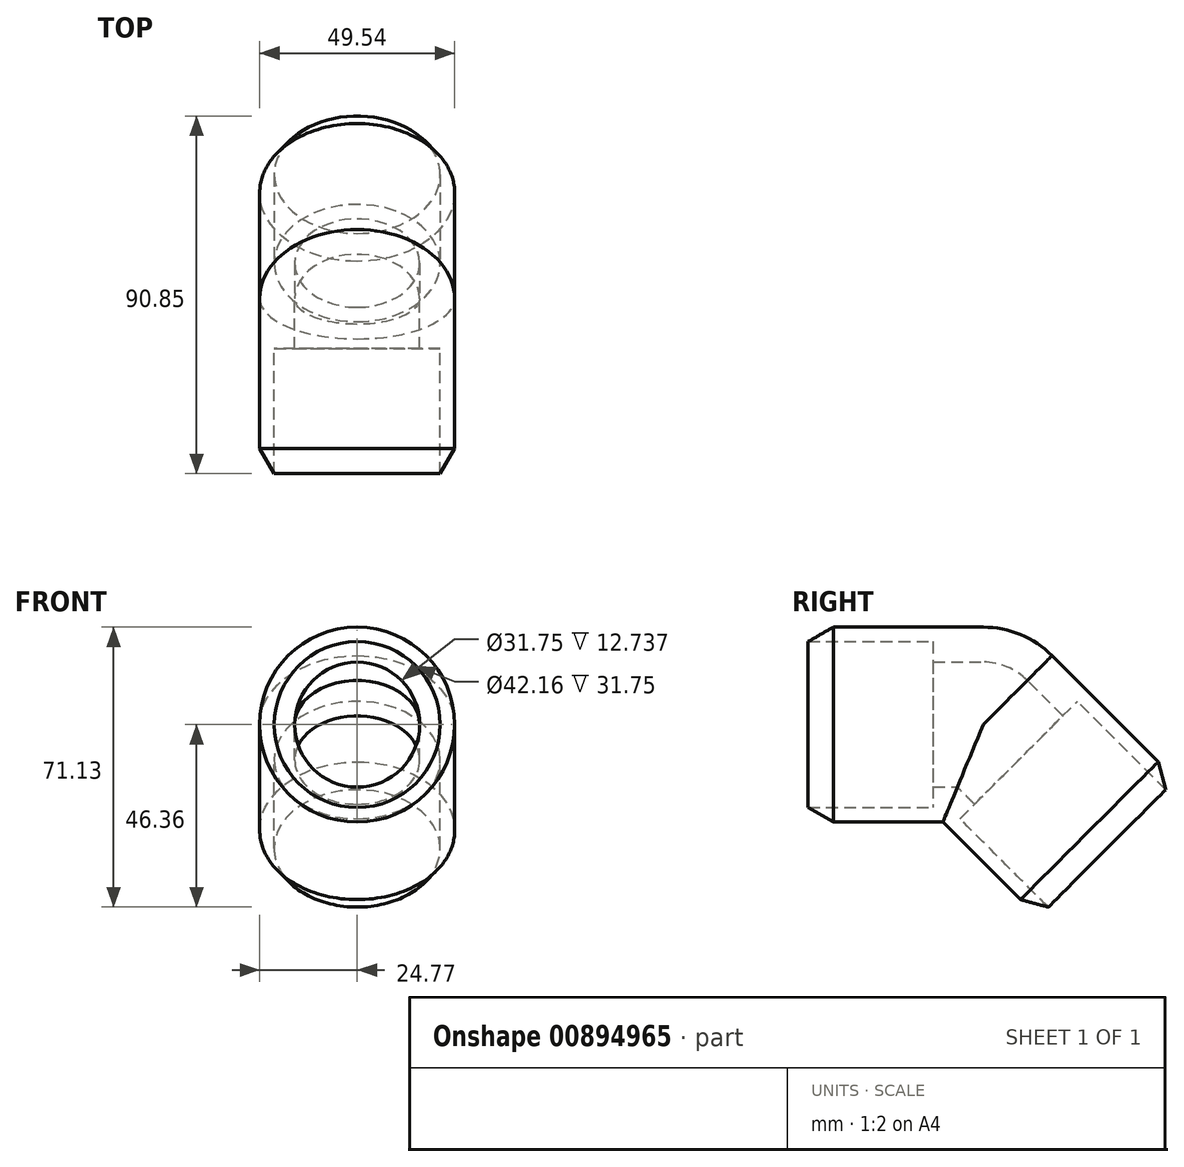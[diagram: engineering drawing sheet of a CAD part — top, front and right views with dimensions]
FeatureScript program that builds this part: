
annotation { "Feature Type Name" : "Feature", "Feature Type Description" : "" }
export const myFeature = defineFeature(function(context is Context, id is Id, definition is map)
    precondition{}
    {
        {
            var Q0;
            Q0=qCreatedBy(makeId("Right.planeOp"),FACE);
            var sketch = newSketch(context, id + "F0", { "sketchPlane" : qUnion([Q0])});
            skLineSegment(sketch, "E0", {"start": v(-44.49, 21.08) * mm, "end": v(-12.74, 21.08) * mm});
            skLineSegment(sketch, "E1", {"start": v(-12.74, 21.08) * mm, "end": v(-12.74, 15.88) * mm});
            skLineSegment(sketch, "E2", {"start": v(-12.74, 15.88) * mm, "end": v(0, 15.88) * mm});
            skLineSegment(sketch, "E3", {"start": v(15.87, 0) * mm, "end": v(15.87, 0) * mm});
            skLineSegment(sketch, "E4", {"start": v(15.87, 0) * mm, "end": v(24.77, 0) * mm});
            skLineSegment(sketch, "E5", {"start": v(24.77, 0) * mm, "end": v(24.77, 0) * mm});
            skLineSegment(sketch, "E6", {"start": v(0, 24.77) * mm, "end": v(-38.1, 24.77) * mm});
            skLineSegment(sketch, "E7", {"start": v(-38.1, 24.76) * mm, "end": v(-44.49, 21.08) * mm});
            skArc(sketch, "E8.filletArc", {"start": v(24.77, 0) * mm, "mid": v(17.51, 17.51) * mm, "end": v(0, 24.77) * mm});
            skArc(sketch, "E9.filletArc", {"start": v(15.88, 0) * mm, "mid": v(11.23, 11.23) * mm, "end": v(0, 15.88) * mm});
            skLineSegment(sketch, "E10", {"start": v(0, 0) * mm, "end": v(0, -11.7) * mm});
            skLineSegment(sketch, "E11", {"start": v(0, 0) * mm, "end": v(10.52, 0) * mm});
            skLineSegment(sketch, "E12", {"start": v(-44.49, 21.08) * mm, "end": v(-44.49, 0) * mm});
            skLineSegment(sketch, "E13", {"start": v(-44.49, 0) * mm, "end": v(15.87, 0) * mm});
            skSolve(sketch);
        }
        {
            var Q0;
            Q0=qCreatedBy(makeId("Right.planeOp"),FACE);
            var sketch = newSketch(context, id + "F1", { "sketchPlane" : qUnion([Q0])});
            skLineSegment(sketch, "E14", {"start": v(16.55, -46.36) * mm, "end": v(-5.9, -23.91) * mm});
            skLineSegment(sketch, "E15", {"start": v(-5.9, -23.91) * mm, "end": v(-2.22, -20.23) * mm});
            skLineSegment(sketch, "E16", {"start": v(-2.22, -20.23) * mm, "end": v(-11.23, -11.23) * mm});
            skLineSegment(sketch, "E17", {"start": v(-11.23, 11.23) * mm, "end": v(-11.23, 11.23) * mm});
            skLineSegment(sketch, "E18", {"start": v(-11.23, 11.23) * mm, "end": v(-17.51, 17.51) * mm});
            skLineSegment(sketch, "E19", {"start": v(-17.51, 17.51) * mm, "end": v(-17.51, 17.51) * mm});
            skLineSegment(sketch, "E20", {"start": v(-17.51, -17.51) * mm, "end": v(9.43, -44.46) * mm});
            skLineSegment(sketch, "E21", {"start": v(9.43, -44.46) * mm, "end": v(16.55, -46.36) * mm});
            skArc(sketch, "E22.filletArc", {"start": v(-17.51, 17.51) * mm, "mid": v(-24.77, 0) * mm, "end": v(-17.51, -17.51) * mm});
            skArc(sketch, "E23.filletArc", {"start": v(-11.23, 11.23) * mm, "mid": v(-15.88, 0) * mm, "end": v(-11.23, -11.23) * mm});
            skLineSegment(sketch, "E24", {"start": v(0, 36.04) * mm, "end": v(0, 0) * mm});
            skLineSegment(sketch, "E25", {"start": v(-2.18, 0) * mm, "end": v(0, 0) * mm});
            skLineSegment(sketch, "E26", {"start": v(16.55, -46.36) * mm, "end": v(31.46, -31.46) * mm});
            skLineSegment(sketch, "E27", {"start": v(31.46, -31.46) * mm, "end": v(-11.23, 11.23) * mm});
            skSolve(sketch);
        }
        {
            var Q0;
            Q0=qSketchRegion(id+"F0",true);
            var Q1;
            Q1=sQuery(id+"F0.wireOp",EDGE,"E13");
            revolve(context, id + "F2", {"surfaceOperationType" : NewSurfaceOperationType.NEW, "entities" : qUnion([Q0]), "axis" : qUnion([Q1]), "revolveType" : RevolveType.FULL});
        }
        {
            var Q0;
            Q0=qSketchRegion(id+"F1",true);
            var Q1;
            Q1=sQuery(id+"F1.wireOp",EDGE,"E27");
            revolve(context, id + "F3", {"operationType" : NewBodyOperationType.ADD, "surfaceOperationType" : NewSurfaceOperationType.NEW, "entities" : qUnion([Q0]), "axis" : qUnion([Q1]), "revolveType" : RevolveType.FULL});
        }
        {
            var Q0;
            Q0=makeQuery(id+"F0.imprint","IMPRINT",FACE,{"disambiguationData":[TD([[makeQuery(id+"F0.imprint","IMPRINT",EDGE,{"derivedFrom":sQuery(id+"F0.wireOp",EDGE,"E0")}),-1.0]])]});
            var Q1;
            Q1=sQuery(id+"F0.wireOp",EDGE,"E13");
            revolve(context, id + "F4", {"operationType" : NewBodyOperationType.REMOVE, "surfaceOperationType" : NewSurfaceOperationType.NEW, "entities" : qUnion([Q0]), "axis" : qUnion([Q1]), "revolveType" : RevolveType.FULL, "oppositeDirection" : true});
        }
        {
            var Q0;
            Q0=makeQuery(id+"F1.imprint","IMPRINT",FACE,{"disambiguationData":[TD([[makeQuery(id+"F1.imprint","IMPRINT",EDGE,{"derivedFrom":sQuery(id+"F1.wireOp",EDGE,"E14")}),-1.0]])]});
            var Q1;
            Q1=sQuery(id+"F1.wireOp",EDGE,"E27");
            revolve(context, id + "F5", {"operationType" : NewBodyOperationType.REMOVE, "surfaceOperationType" : NewSurfaceOperationType.NEW, "entities" : qUnion([Q0]), "axis" : qUnion([Q1]), "revolveType" : RevolveType.FULL, "oppositeDirection" : true});
        }
    });
